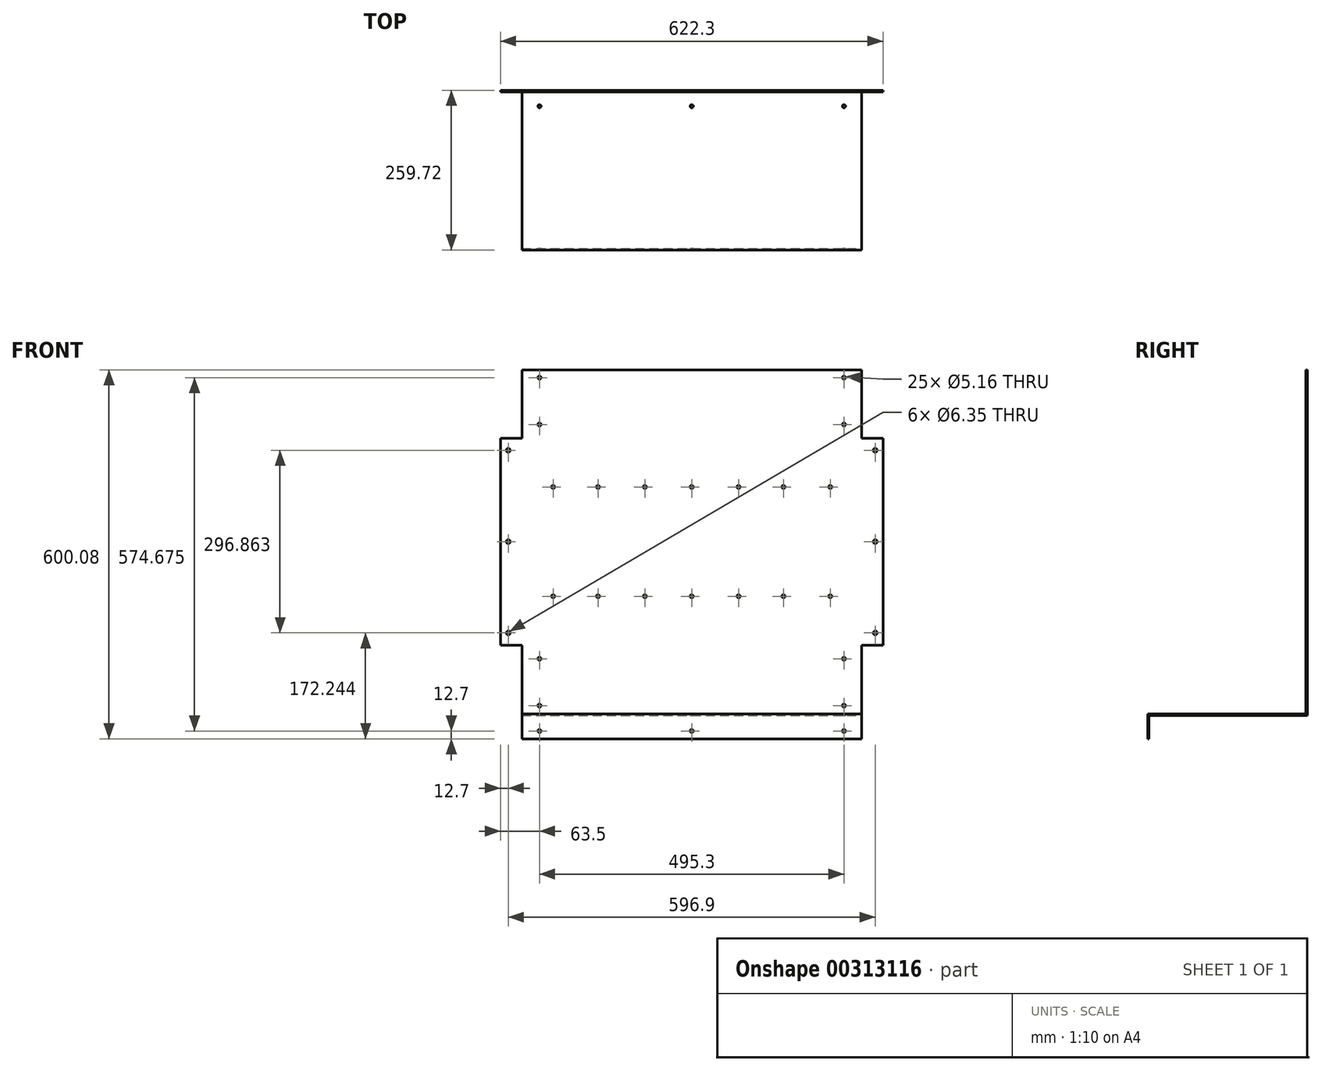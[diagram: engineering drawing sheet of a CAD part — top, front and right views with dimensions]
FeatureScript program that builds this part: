
annotation { "Feature Type Name" : "Feature", "Feature Type Description" : "" }
export const myFeature = defineFeature(function(context is Context, id is Id, definition is map)
    precondition{}
    {
        {
            var Q0;
            Q0=qCreatedBy(makeId("Front.planeOp"),FACE);
            var sketch = newSketch(context, id + "F0", { "sketchPlane" : qUnion([Q0])});
            skLineSegment(sketch, "E0.bottom", {"start": v(587.37, 447.68) * mm, "end": v(34.92, 447.68) * mm});
            skLineSegment(sketch, "E0.top", {"start": v(622.3, 0) * mm, "end": v(587.37, 0) * mm});
            skLineSegment(sketch, "E0.left", {"start": v(622.3, 336.55) * mm, "end": v(622.3, 0) * mm});
            skLineSegment(sketch, "E0.right", {"start": v(0, 336.55) * mm, "end": v(0, 0) * mm});
            skPoint(sketch, "E0.middle", {"position": v(0, 0) * mm});
            skLineSegment(sketch, "E1.top", {"start": v(622.3, 336.55) * mm, "end": v(587.37, 336.55) * mm});
            skLineSegment(sketch, "E1.right", {"start": v(587.37, 447.68) * mm, "end": v(587.37, 336.55) * mm});
            skLineSegment(sketch, "E2.top", {"start": v(0, 336.55) * mm, "end": v(34.92, 336.55) * mm});
            skLineSegment(sketch, "E2.right", {"start": v(34.92, 447.68) * mm, "end": v(34.92, 336.55) * mm});
            skLineSegment(sketch, "E3", {"start": v(587.37, 0) * mm, "end": v(587.37, -114.3) * mm});
            skLineSegment(sketch, "E4", {"start": v(587.37, -114.3) * mm, "end": v(34.93, -114.3) * mm});
            skLineSegment(sketch, "E5", {"start": v(34.93, -114.3) * mm, "end": v(34.93, 0) * mm});
            skLineSegment(sketch, "E6.trimOffspring", {"start": v(34.93, 0) * mm, "end": v(0, 0) * mm});
            skSolve(sketch);
        }
        {
            var Q0;
            Q0 = qSketchRegion(id + "F0", true);
            extrude(context, id + "F1", {"entities" : qUnion([Q0]), "depth" : 2.54 * mm});
        }
        {
            var Q0;
            Q0=makeQuery(id+"F1.opExtrude","CAP_FACE",FACE,{"disambiguationData":[OSD([sQuery(id+"F0.wireOp",EDGE,"E0.bottom"),sQuery(id+"F0.wireOp",EDGE,"E0.top"),sQuery(id+"F0.wireOp",EDGE,"E0.left"),sQuery(id+"F0.wireOp",EDGE,"E0.right"),sQuery(id+"F0.wireOp",EDGE,"E1.top"),sQuery(id+"F0.wireOp",EDGE,"E1.right"),sQuery(id+"F0.wireOp",EDGE,"E2.top"),sQuery(id+"F0.wireOp",EDGE,"E2.right")])],"isStart":true});
            var sketch = newSketch(context, id + "F2", { "sketchPlane" : qUnion([Q0])});
            skPoint(sketch, "E7.centerSnap0", {"position": v(-604.84, 0) * mm});
            skCircle(sketch, "E8", {"center": v(-558.8, 434.98) * mm, "radius": 2.58 * mm});
            skCircle(sketch, "E9", {"center": v(-558.8, 358.78) * mm, "radius": 2.58 * mm});
            skCircle(sketch, "E10", {"center": v(-63.5, 358.78) * mm, "radius": 2.58 * mm});
            skCircle(sketch, "E11", {"center": v(-63.5, 434.98) * mm, "radius": 2.58 * mm});
            skCircle(sketch, "E12", {"center": v(-609.6, 316.7) * mm, "radius": 3.18 * mm});
            skCircle(sketch, "E13", {"center": v(-609.6, 168.28) * mm, "radius": 3.18 * mm});
            skCircle(sketch, "E14", {"center": v(-609.6, 19.84) * mm, "radius": 3.18 * mm});
            skCircle(sketch, "E15", {"center": v(-12.7, 19.84) * mm, "radius": 3.18 * mm});
            skCircle(sketch, "E16", {"center": v(-12.7, 168.28) * mm, "radius": 3.18 * mm});
            skCircle(sketch, "E17", {"center": v(-12.7, 316.7) * mm, "radius": 3.18 * mm});
            skLineSegment(sketch, "E18", {"start": v(-609.6, 19.84) * mm, "end": v(-609.6, 316.7) * mm, "construction": true});
            skCircle(sketch, "E19", {"center": v(-558.8, -22.22) * mm, "radius": 2.58 * mm});
            skCircle(sketch, "E20", {"center": v(-558.8, -98.42) * mm, "radius": 2.58 * mm});
            skCircle(sketch, "E21", {"center": v(-63.5, -98.42) * mm, "radius": 2.58 * mm});
            skCircle(sketch, "E22", {"center": v(-63.5, -22.22) * mm, "radius": 2.58 * mm});
            skPoint(sketch, "E23.centerSnap0", {"position": v(-311.15, 447.68) * mm});
            skCircle(sketch, "E24", {"center": v(-85.72, 257.18) * mm, "radius": 2.58 * mm});
            skCircle(sketch, "E25", {"center": v(-536.57, 257.18) * mm, "radius": 2.58 * mm});
            skLineSegment(sketch, "E26", {"start": v(-85.72, 257.18) * mm, "end": v(-536.57, 257.18) * mm, "construction": true});
            skPoint(sketch, "E27", {"position": v(-311.15, 257.18) * mm});
            skCircle(sketch, "E28", {"center": v(-234.95, 257.18) * mm, "radius": 2.58 * mm});
            skCircle(sketch, "E29", {"center": v(-387.35, 257.18) * mm, "radius": 2.58 * mm});
            skLineSegment(sketch, "E30.direction1", {"start": v(-536.57, 257.18) * mm, "end": v(-387.35, 257.18) * mm, "construction": true});
            skCircle(sketch, "E31", {"center": v(-311.15, 257.18) * mm, "radius": 2.58 * mm});
            skCircle(sketch, "E32", {"center": v(-158.75, 257.18) * mm, "radius": 2.58 * mm});
            skCircle(sketch, "E33", {"center": v(-460.37, 257.18) * mm, "radius": 2.58 * mm});
            skLineSegment(sketch, "E34.0.1.0", {"start": v(-85.72, 79.37) * mm, "end": v(-536.57, 79.37) * mm, "construction": true});
            skLineSegment(sketch, "E34.0.1.1", {"start": v(-536.57, 79.37) * mm, "end": v(-387.35, 79.37) * mm, "construction": true});
            skPoint(sketch, "E34.0.1.2", {"position": v(-311.15, 79.37) * mm});
            skCircle(sketch, "E34.0.1.3", {"center": v(-460.37, 79.37) * mm, "radius": 2.58 * mm});
            skCircle(sketch, "E34.0.1.4", {"center": v(-234.95, 79.37) * mm, "radius": 2.58 * mm});
            skCircle(sketch, "E34.0.1.5", {"center": v(-158.75, 79.37) * mm, "radius": 2.58 * mm});
            skCircle(sketch, "E34.0.1.6", {"center": v(-85.72, 79.37) * mm, "radius": 2.58 * mm});
            skCircle(sketch, "E34.0.1.7", {"center": v(-387.35, 79.38) * mm, "radius": 2.58 * mm});
            skCircle(sketch, "E34.0.1.8", {"center": v(-311.15, 79.37) * mm, "radius": 2.58 * mm});
            skCircle(sketch, "E34.0.1.9", {"center": v(-536.57, 79.37) * mm, "radius": 2.58 * mm});
            skLineSegment(sketch, "E34.direction1", {"start": v(-536.57, 257.18) * mm, "end": v(-311.15, 257.18) * mm, "construction": true});
            skLineSegment(sketch, "E34.direction2", {"start": v(-536.57, 257.18) * mm, "end": v(-536.57, 79.37) * mm, "construction": true});
            skSolve(sketch);
        }
        {
            var Q0;
            Q0 = qSketchRegion(id + "F2", true);
            extrude(context, id + "F3", {"entities" : qUnion([Q0]), "operationType" : NewBodyOperationType.REMOVE, "endBound" : BoundingType.THROUGH_ALL, "oppositeDirection" : true, "depth" : 25.4 * mm});
        }
        {
            var Q0;
            Q0=makeQuery(id+"F1.opExtrude","CAP_FACE",FACE,{"disambiguationData":[OSD([sQuery(id+"F0.wireOp",EDGE,"E0.bottom"),sQuery(id+"F0.wireOp",EDGE,"E0.top"),sQuery(id+"F0.wireOp",EDGE,"E0.left"),sQuery(id+"F0.wireOp",EDGE,"E0.right"),sQuery(id+"F0.wireOp",EDGE,"E1.top"),sQuery(id+"F0.wireOp",EDGE,"E1.right"),sQuery(id+"F0.wireOp",EDGE,"E2.top"),sQuery(id+"F0.wireOp",EDGE,"E2.right")])],"isStart":false});
            var sketch = newSketch(context, id + "F4", { "sketchPlane" : qUnion([Q0])});
            skLineSegment(sketch, "E35.bottom", {"start": v(587.37, -114.3) * mm, "end": v(34.93, -114.3) * mm});
            skLineSegment(sketch, "E35.top", {"start": v(587.37, -111.76) * mm, "end": v(34.93, -111.76) * mm});
            skLineSegment(sketch, "E35.left", {"start": v(587.37, -114.3) * mm, "end": v(587.37, -111.76) * mm});
            skLineSegment(sketch, "E35.right", {"start": v(34.93, -114.3) * mm, "end": v(34.93, -111.76) * mm});
            skSolve(sketch);
        }
        {
            var Q0;
            Q0 = qSketchRegion(id + "F4", true);
            extrude(context, id + "F5", {"entities" : qUnion([Q0]), "operationType" : NewBodyOperationType.ADD, "depth" : 257.18 * mm});
        }
        {
            var Q0;
            Q0=makeQuery(id+"F5.boolean.opBoolean","MERGE",FACE,{"derivedFrom":[makeQuery(id+"F1.opExtrude","SWEPT_FACE",FACE,{"disambiguationData":[OSD([sQuery(id+"F0.wireOp",EDGE,"E4")])]}),makeQuery(id+"F5.opExtrude","SWEPT_FACE",FACE,{"disambiguationData":[OSD([sQuery(id+"F4.wireOp",EDGE,"E35.bottom")])]})]});
            var sketch = newSketch(context, id + "F6", { "sketchPlane" : qUnion([Q0])});
            skLineSegment(sketch, "E36.bottom", {"start": v(34.92, 259.72) * mm, "end": v(587.37, 259.72) * mm});
            skLineSegment(sketch, "E36.top", {"start": v(34.92, 257.18) * mm, "end": v(587.37, 257.18) * mm});
            skLineSegment(sketch, "E36.left", {"start": v(34.92, 259.72) * mm, "end": v(34.92, 257.18) * mm});
            skLineSegment(sketch, "E36.right", {"start": v(587.37, 259.72) * mm, "end": v(587.37, 257.18) * mm});
            skSolve(sketch);
        }
        {
            var Q0;
            Q0 = qSketchRegion(id + "F6", true);
            extrude(context, id + "F7", {"entities" : qUnion([Q0]), "operationType" : NewBodyOperationType.ADD, "depth" : 38.1 * mm});
        }
        {
            var Q0;
            Q0=makeQuery(id+"F7.boolean.opBoolean","MERGE",FACE,{"derivedFrom":[makeQuery(id+"F5.opExtrude","CAP_FACE",FACE,{"disambiguationData":[OSD([sQuery(id+"F4.wireOp",EDGE,"E35.bottom"),sQuery(id+"F4.wireOp",EDGE,"E35.top"),sQuery(id+"F4.wireOp",EDGE,"E35.left"),sQuery(id+"F4.wireOp",EDGE,"E35.right")])],"isStart":false}),makeQuery(id+"F7.opExtrude","SWEPT_FACE",FACE,{"disambiguationData":[OSD([sQuery(id+"F6.wireOp",EDGE,"E36.bottom")])]})]});
            var sketch = newSketch(context, id + "F8", { "sketchPlane" : qUnion([Q0])});
            skCircle(sketch, "E37", {"center": v(311.15, -139.7) * mm, "radius": 2.58 * mm});
            skPoint(sketch, "E37.centerSnap0", {"position": v(311.15, -152.4) * mm});
            skCircle(sketch, "E38", {"center": v(558.8, -139.7) * mm, "radius": 2.58 * mm});
            skCircle(sketch, "E39", {"center": v(63.5, -139.7) * mm, "radius": 2.58 * mm});
            skSolve(sketch);
        }
        {
            var Q0;
            Q0 = qSketchRegion(id + "F8", true);
            extrude(context, id + "F9", {"entities" : qUnion([Q0]), "operationType" : NewBodyOperationType.REMOVE, "endBound" : BoundingType.THROUGH_ALL, "oppositeDirection" : true, "depth" : 25.4 * mm});
        }
        {
            var Q0;
            Q0=makeQuery(id+"F5.boolean.opBoolean","MERGE",FACE,{"derivedFrom":[makeQuery(id+"F1.opExtrude","SWEPT_FACE",FACE,{"disambiguationData":[OSD([sQuery(id+"F0.wireOp",EDGE,"E4")])]}),makeQuery(id+"F5.opExtrude","SWEPT_FACE",FACE,{"disambiguationData":[OSD([sQuery(id+"F4.wireOp",EDGE,"E35.bottom")])]})]});
            var sketch = newSketch(context, id + "F10", { "sketchPlane" : qUnion([Q0])});
            skCircle(sketch, "E40", {"center": v(311.15, 26.04) * mm, "radius": 2.58 * mm});
            skPoint(sketch, "E40.centerSnap0", {"position": v(311.15, 0) * mm});
            skCircle(sketch, "E41", {"center": v(558.8, 26.04) * mm, "radius": 2.58 * mm});
            skCircle(sketch, "E42", {"center": v(63.5, 26.04) * mm, "radius": 2.58 * mm});
            skSolve(sketch);
        }
        {
            var Q0;
            Q0 = qSketchRegion(id + "F10", true);
            extrude(context, id + "F11", {"entities" : qUnion([Q0]), "operationType" : NewBodyOperationType.REMOVE, "endBound" : BoundingType.THROUGH_ALL, "oppositeDirection" : true, "depth" : 25.4 * mm});
        }
    });
